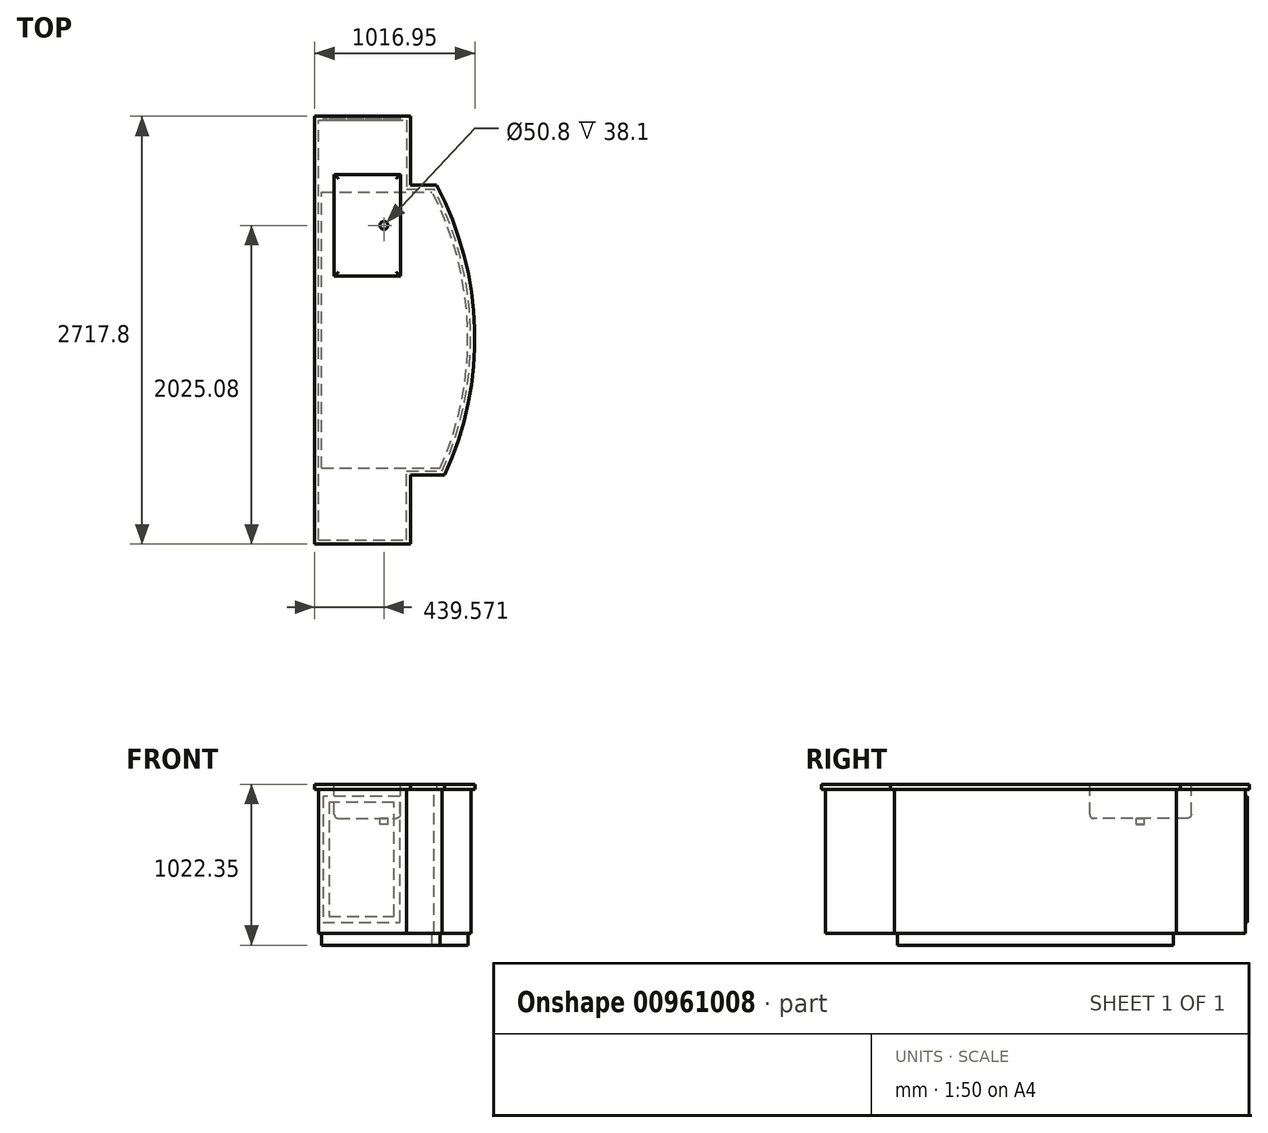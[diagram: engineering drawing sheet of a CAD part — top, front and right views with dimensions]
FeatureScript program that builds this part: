
annotation { "Feature Type Name" : "Feature", "Feature Type Description" : "" }
export const myFeature = defineFeature(function(context is Context, id is Id, definition is map)
    precondition{}
    {
        {
            var Q0;
            Q0=qCreatedBy(makeId("Top.planeOp"),FACE);
            var sketch = newSketch(context, id + "F0", { "sketchPlane" : qUnion([Q0])});
            skLineSegment(sketch, "E0", {"start": v(-306.4, -542.54) * mm, "end": v(303.2, -542.54) * mm});
            skLineSegment(sketch, "E1", {"start": v(-306.4, -542.54) * mm, "end": v(-306.4, 2175.26) * mm});
            skLineSegment(sketch, "E2", {"start": v(303.2, -542.54) * mm, "end": v(303.2, -104.39) * mm});
            skLineSegment(sketch, "E3", {"start": v(303.2, -104.39) * mm, "end": v(519.38, -104.39) * mm});
            skArc(sketch, "E4", {"start": v(519.38, -104.39) * mm, "mid": v(709.72, 822.47) * mm, "end": v(467.36, 1737.11) * mm});
            skLineSegment(sketch, "E5", {"start": v(-306.4, 2175.26) * mm, "end": v(303.2, 2175.26) * mm});
            skLineSegment(sketch, "E6", {"start": v(303.2, 2175.26) * mm, "end": v(303.2, 1737.11) * mm});
            skLineSegment(sketch, "E7", {"start": v(303.2, 1737.11) * mm, "end": v(467.36, 1737.11) * mm});
            skSolve(sketch);
        }
        {
            var Q0;
            Q0 = qSketchRegion(id + "F0", true);
            extrude(context, id + "F1", {"entities" : qUnion([Q0]), "depth" : 31.75 * mm, "offsetDistance" : 25.4 * mm});
        }
        {
            var Q0;
            Q0=makeQuery(id+"F1.opExtrude","CAP_FACE",FACE,{"disambiguationData":[OSD([sQuery(id+"F0.wireOp",EDGE,"E0"),sQuery(id+"F0.wireOp",EDGE,"E1"),sQuery(id+"F0.wireOp",EDGE,"E2"),sQuery(id+"F0.wireOp",EDGE,"E3"),sQuery(id+"F0.wireOp",EDGE,"E4"),sQuery(id+"F0.wireOp",EDGE,"E5"),sQuery(id+"F0.wireOp",EDGE,"E6"),sQuery(id+"F0.wireOp",EDGE,"E7")])],"isStart":true});
            var sketch = newSketch(context, id + "F2", { "sketchPlane" : qUnion([Q0])});
            skLineSegment(sketch, "E8.0", {"start": v(-306.4, 542.54) * mm, "end": v(303.2, 542.54) * mm});
            skLineSegment(sketch, "E9.0", {"start": v(-306.4, 542.54) * mm, "end": v(-306.4, -2175.26) * mm});
            skLineSegment(sketch, "E10.0", {"start": v(303.2, 542.54) * mm, "end": v(303.2, 104.39) * mm});
            skLineSegment(sketch, "E11.0", {"start": v(303.2, 104.39) * mm, "end": v(519.38, 104.39) * mm});
            skArc(sketch, "E12.0", {"start": v(519.38, 104.39) * mm, "mid": v(709.72, -822.47) * mm, "end": v(467.36, -1737.11) * mm});
            skPoint(sketch, "E13.0", {"position": v(385.28, -1737.11) * mm});
            skLineSegment(sketch, "E14.0", {"start": v(303.2, -1737.11) * mm, "end": v(467.36, -1737.11) * mm});
            skLineSegment(sketch, "E15.0", {"start": v(303.2, -2175.26) * mm, "end": v(303.2, -1737.11) * mm});
            skLineSegment(sketch, "E16.0", {"start": v(-306.4, -2175.26) * mm, "end": v(303.2, -2175.26) * mm});
            skLineSegment(sketch, "E17.0", {"start": v(-281, 517.14) * mm, "end": v(277.8, 517.14) * mm});
            skLineSegment(sketch, "E17.1", {"start": v(277.8, 517.14) * mm, "end": v(277.8, 78.99) * mm});
            skLineSegment(sketch, "E17.2", {"start": v(-281, 517.14) * mm, "end": v(-281, -2149.86) * mm});
            skLineSegment(sketch, "E17.3", {"start": v(277.8, 78.99) * mm, "end": v(503.07, 78.99) * mm});
            skLineSegment(sketch, "E17.4", {"start": v(-281, -2149.86) * mm, "end": v(277.8, -2149.86) * mm});
            skLineSegment(sketch, "E17.5", {"start": v(277.8, -2149.86) * mm, "end": v(277.8, -1711.71) * mm});
            skLineSegment(sketch, "E17.6", {"start": v(277.8, -1711.71) * mm, "end": v(452.06, -1711.71) * mm});
            skArc(sketch, "E17.7", {"start": v(503.07, 78.99) * mm, "mid": v(684.31, -822.25) * mm, "end": v(452.06, -1711.71) * mm});
            skArc(sketch, "E18", {"start": v(563.6, -69.94) * mm, "mid": v(569.29, -50.91) * mm, "end": v(552.58, -40.17) * mm});
            skArc(sketch, "E19.1.0.0", {"start": v(589, -69.94) * mm, "mid": v(594.69, -50.91) * mm, "end": v(577.98, -40.17) * mm});
            skArc(sketch, "E19.2.0.0", {"start": v(614.4, -69.94) * mm, "mid": v(620.09, -50.91) * mm, "end": v(603.38, -40.17) * mm});
            skLineSegment(sketch, "E19.direction1", {"start": v(563.6, -69.94) * mm, "end": v(589, -69.94) * mm, "construction": true});
            skSolve(sketch);
        }
        {
            var Q0;
            Q0=makeQuery(id+"F2.imprint","IMPRINT",FACE,{"disambiguationData":[TD([[makeQuery(id+"F2.imprint","IMPRINT",EDGE,{"derivedFrom":sQuery(id+"F2.wireOp",EDGE,"E17.0")}),-1.0]])]});
            extrude(context, id + "F3", {"entities" : qUnion([Q0]), "operationType" : NewBodyOperationType.ADD, "depth" : 914.4 * mm, "offsetDistance" : 25.4 * mm});
        }
        {
            var Q0;
            Q0=makeQuery(id+"F3.opExtrude","CAP_FACE",FACE,{"disambiguationData":[OSD([sQuery(id+"F2.wireOp",EDGE,"E17.0"),sQuery(id+"F2.wireOp",EDGE,"E17.1"),sQuery(id+"F2.wireOp",EDGE,"E17.2"),sQuery(id+"F2.wireOp",EDGE,"E17.3"),sQuery(id+"F2.wireOp",EDGE,"E17.4"),sQuery(id+"F2.wireOp",EDGE,"E17.5"),sQuery(id+"F2.wireOp",EDGE,"E17.6"),sQuery(id+"F2.wireOp",EDGE,"E17.7")])],"isStart":false});
            var sketch = newSketch(context, id + "F4", { "sketchPlane" : qUnion([Q0])});
            skLineSegment(sketch, "E20.0", {"start": v(-306.4, 542.54) * mm, "end": v(303.2, 542.54) * mm});
            skLineSegment(sketch, "E21.0", {"start": v(-306.4, 542.54) * mm, "end": v(-306.4, -2175.26) * mm});
            skLineSegment(sketch, "E22.0", {"start": v(303.2, 542.54) * mm, "end": v(303.2, 104.39) * mm});
            skLineSegment(sketch, "E23.0", {"start": v(303.2, 104.39) * mm, "end": v(519.38, 104.39) * mm});
            skArc(sketch, "E24.0", {"start": v(519.38, 104.39) * mm, "mid": v(709.72, -822.47) * mm, "end": v(467.36, -1737.11) * mm});
            skPoint(sketch, "E25.0", {"position": v(385.28, -1737.11) * mm});
            skLineSegment(sketch, "E26.0", {"start": v(303.2, -1737.11) * mm, "end": v(467.36, -1737.11) * mm});
            skLineSegment(sketch, "E27.0", {"start": v(303.2, -2175.26) * mm, "end": v(303.2, -1737.11) * mm});
            skLineSegment(sketch, "E28.0", {"start": v(-306.4, -2175.26) * mm, "end": v(303.2, -2175.26) * mm});
            skLineSegment(sketch, "E29.0", {"start": v(-281, 517.14) * mm, "end": v(277.8, 517.14) * mm});
            skLineSegment(sketch, "E29.1", {"start": v(277.8, 517.14) * mm, "end": v(277.8, 78.99) * mm});
            skLineSegment(sketch, "E29.2", {"start": v(-281, 517.14) * mm, "end": v(-281, -2149.86) * mm});
            skLineSegment(sketch, "E29.3", {"start": v(277.8, 78.99) * mm, "end": v(503.07, 78.99) * mm});
            skLineSegment(sketch, "E29.4", {"start": v(-281, -2149.86) * mm, "end": v(277.8, -2149.86) * mm});
            skLineSegment(sketch, "E29.5", {"start": v(277.8, -2149.86) * mm, "end": v(277.8, -1711.71) * mm});
            skLineSegment(sketch, "E29.6", {"start": v(277.8, -1711.71) * mm, "end": v(452.06, -1711.71) * mm});
            skArc(sketch, "E29.7", {"start": v(503.07, 78.99) * mm, "mid": v(684.31, -822.25) * mm, "end": v(452.06, -1711.71) * mm});
            skPoint(sketch, "E30.0", {"position": v(-306.4, -2175.26) * mm});
            skLineSegment(sketch, "E31.0", {"start": v(-261.96, 59.94) * mm, "end": v(-261.96, -1692.66) * mm});
            skLineSegment(sketch, "E31.1", {"start": v(-261.96, 59.94) * mm, "end": v(490.75, 59.94) * mm});
            skArc(sketch, "E31.2", {"start": v(490.75, 59.94) * mm, "mid": v(665.26, -822.09) * mm, "end": v(440.5, -1692.66) * mm});
            skLineSegment(sketch, "E31.3", {"start": v(-261.96, -1692.66) * mm, "end": v(440.5, -1692.66) * mm});
            skSolve(sketch);
        }
        {
            var Q0;
            Q0=makeQuery(id+"F4.imprint","IMPRINT",FACE,{"disambiguationData":[TD([[makeQuery(id+"F4.imprint","IMPRINT",EDGE,{"derivedFrom":sQuery(id+"F4.wireOp",EDGE,"E31.0")}),1.0]])]});
            extrude(context, id + "F5", {"entities" : qUnion([Q0]), "operationType" : NewBodyOperationType.ADD, "depth" : 76.2 * mm, "offsetDistance" : 25.4 * mm});
        }
        {
            var Q0;
            Q0=makeQuery(id+"F3.opExtrude","SWEPT_FACE",FACE,{"disambiguationData":[OSD([sQuery(id+"F2.wireOp",EDGE,"E17.4")])]});
            var sketch = newSketch(context, id + "F6", { "sketchPlane" : qUnion([Q0])});
            skLineSegment(sketch, "E32", {"start": v(-235.48, -44.6) * mm, "end": v(253.92, -44.6) * mm});
            skLineSegment(sketch, "E33", {"start": v(253.92, -44.6) * mm, "end": v(253.92, -844.7) * mm});
            skLineSegment(sketch, "E34", {"start": v(253.92, -844.7) * mm, "end": v(-235.48, -844.7) * mm});
            skLineSegment(sketch, "E35", {"start": v(-235.48, -844.7) * mm, "end": v(-235.48, -44.6) * mm});
            skLineSegment(sketch, "E36.0", {"start": v(-197.38, -806.6) * mm, "end": v(-197.38, -82.7) * mm});
            skLineSegment(sketch, "E36.1", {"start": v(215.82, -806.6) * mm, "end": v(-197.38, -806.6) * mm});
            skLineSegment(sketch, "E36.2", {"start": v(215.82, -82.7) * mm, "end": v(215.82, -806.6) * mm});
            skLineSegment(sketch, "E36.3", {"start": v(-197.38, -82.7) * mm, "end": v(215.82, -82.7) * mm});
            skSolve(sketch);
        }
        {
            var Q0;
            Q0=makeQuery(id+"F6.imprint","IMPRINT",FACE,{"disambiguationData":[TD([[makeQuery(id+"F6.imprint","IMPRINT",EDGE,{"derivedFrom":sQuery(id+"F6.wireOp",EDGE,"E32")}),-1.0]])]});
            extrude(context, id + "F7", {"entities" : qUnion([Q0]), "operationType" : NewBodyOperationType.ADD, "depth" : 12.7 * mm, "offsetDistance" : 25.4 * mm});
        }
        {
            var Q0;
            Q0=makeQuery(id+"F1.opExtrude","CAP_FACE",FACE,{"disambiguationData":[OSD([sQuery(id+"F0.wireOp",EDGE,"E0"),sQuery(id+"F0.wireOp",EDGE,"E1"),sQuery(id+"F0.wireOp",EDGE,"E2"),sQuery(id+"F0.wireOp",EDGE,"E3"),sQuery(id+"F0.wireOp",EDGE,"E4"),sQuery(id+"F0.wireOp",EDGE,"E5"),sQuery(id+"F0.wireOp",EDGE,"E6"),sQuery(id+"F0.wireOp",EDGE,"E7")])],"isStart":false});
            var sketch = newSketch(context, id + "F8", { "sketchPlane" : qUnion([Q0])});
            skLineSegment(sketch, "E37.bottom", {"start": v(-182.45, 1805) * mm, "end": v(237.5, 1805) * mm});
            skLineSegment(sketch, "E37.top", {"start": v(-182.45, 1160.07) * mm, "end": v(237.5, 1160.07) * mm});
            skLineSegment(sketch, "E37.left", {"start": v(-182.45, 1805) * mm, "end": v(-182.45, 1160.07) * mm});
            skLineSegment(sketch, "E37.right", {"start": v(237.5, 1805) * mm, "end": v(237.5, 1160.07) * mm});
            skLineSegment(sketch, "E38", {"start": v(-182.45, 1482.54) * mm, "end": v(448.78, 1482.54) * mm, "construction": true});
            skCircle(sketch, "E39", {"center": v(330.48, 1482.54) * mm, "radius": 44.45 * mm, "construction": true});
            skCircle(sketch, "E40", {"center": v(330.48, 1639.88) * mm, "radius": 19.05 * mm, "construction": true});
            skLineSegment(sketch, "E41", {"start": v(330.48, 1482.54) * mm, "end": v(330.48, 1288.4) * mm});
            skLineSegment(sketch, "E42.MirrorCS", {"start": v(330.48, 1482.54) * mm, "end": v(330.48, 1676.67) * mm, "construction": true});
            skCircle(sketch, "E43.MirrorC", {"center": v(330.48, 1325.19) * mm, "radius": 19.05 * mm, "construction": true});
            skSolve(sketch);
        }
        {
            var Q0;
            Q0=makeQuery(id+"F8.imprint","IMPRINT",FACE,{"disambiguationData":[TD([[makeQuery(id+"F8.imprint","IMPRINT",EDGE,{"derivedFrom":sQuery(id+"F8.wireOp",EDGE,"E37.bottom")}),-1.0]])]});
            extrude(context, id + "F9", {"entities" : qUnion([Q0]), "operationType" : NewBodyOperationType.REMOVE, "oppositeDirection" : true, "depth" : 215.9 * mm, "offsetDistance" : 25.4 * mm});
        }
        {
            var Q0;
            Q0=makeQuery(id+"F9.boolean.opBoolean","COPY",EDGE,{"derivedFrom":makeQuery(id+"F9.opExtrude","CAP_EDGE",EDGE,{"disambiguationData":[OSD([sQuery(id+"F8.wireOp",EDGE,"E37.bottom")])],"isStart":false})});
            var Q1;
            Q1=makeQuery(id+"F9.boolean.opBoolean","COPY",EDGE,{"derivedFrom":makeQuery(id+"F9.opExtrude","CAP_EDGE",EDGE,{"disambiguationData":[OSD([sQuery(id+"F8.wireOp",EDGE,"E37.left")])],"isStart":false})});
            var Q2;
            Q2=makeQuery(id+"F9.boolean.opBoolean","COPY",EDGE,{"derivedFrom":makeQuery(id+"F9.opExtrude","CAP_EDGE",EDGE,{"disambiguationData":[OSD([sQuery(id+"F8.wireOp",EDGE,"E37.right")])],"isStart":false})});
            var Q3;
            Q3=makeQuery(id+"F9.boolean.opBoolean","COPY",EDGE,{"derivedFrom":makeQuery(id+"F9.opExtrude","CAP_EDGE",EDGE,{"disambiguationData":[OSD([sQuery(id+"F8.wireOp",EDGE,"E37.top")])],"isStart":false})});
            fillet(context, id + "F10", {"entities" : qUnion([Q0, Q1, Q2, Q3]), "radius" : 25.4 * mm, "tangentPropagation" : true, "allowEdgeOverflow" : false});
        }
        {
            var Q0;
            Q0=makeQuery(id+"F9.boolean.opBoolean","COPY",FACE,{"derivedFrom":makeQuery(id+"F9.opExtrude","CAP_FACE",FACE,{"disambiguationData":[OSD([sQuery(id+"F8.wireOp",EDGE,"E37.bottom"),sQuery(id+"F8.wireOp",EDGE,"E37.top"),sQuery(id+"F8.wireOp",EDGE,"E37.left"),sQuery(id+"F8.wireOp",EDGE,"E37.right")])],"isStart":false})});
            var sketch = newSketch(context, id + "F11", { "sketchPlane" : qUnion([Q0])});
            skLineSegment(sketch, "E44.0", {"start": v(-182.45, 1482.54) * mm, "end": v(448.78, 1482.54) * mm, "construction": true});
            skCircle(sketch, "E45", {"center": v(133.16, 1482.54) * mm, "radius": 25.4 * mm});
            skSolve(sketch);
        }
        {
            var Q0;
            Q0 = qSketchRegion(id + "F11", true);
            extrude(context, id + "F12", {"entities" : qUnion([Q0]), "operationType" : NewBodyOperationType.REMOVE, "oppositeDirection" : true, "depth" : 38.1 * mm, "offsetDistance" : 25.4 * mm});
        }
    });
